# Revit family: Furniture_Chair_YUMI_3
name_source: partatom
category: Furniture
units: mm (PartAtom-declared; Revit-internal decimal feet)

## family parameters
Always vertical = No
Cut with Voids When Loaded = No
OmniClass Number = 23.21.23.15.17
Room Calculation Point = No
Shared = No
Work Plane-Based = Yes

## types (6) — shared parameters
BIMobject category = Chair
BIMobject category code = furniture-chair
BIMobject main category = Furniture
BIMobject main category code = furniture
Brand url = https://www.sandlerseating.com
Default Elevation = 1219.2 mm  [stored 4 ft]
Description = Chair
Design country = UK
Edition number = 1
Heigth Shell = 740 mm  [stored 2.42782 ft]
IFC Classification = Furnishing Element
Manufacturer = Sandler
Manufacturer country = UK
Manufacturer name = Sandler
Masterformat 2014 Code = 12 48 43.13
Masterformat 2014 Description = Chair Mats
OmniClass Code = 23-21 23 15 17
Product Guid = ??
Product data url = https://www.sandlerseating.com
Product family = Furniture
Product group = Chair
Seat = TP01 - YUMI
Uniformat II Description = Movable Furnishings
height = 1020 mm  [stored 3.34646 ft]

## per-type parameters (varying)
| type | Frame | Frame Material | Seat Material | Shell Material | depth | width |
| YUMI 3.6 | BS04 - YUMI | Wood - Wenge Beech | Laminate - Grey | Laminate - Grey | 550 mm | 590 mm  [stored 1.9357 ft] |
| YUMI 3.5 | BS04 - YUMI | Wood - Natural Beech | Leather - Blue - Sandler 145 | Leather - Blue - Sandler 145 | 550 mm | 590 mm  [stored 1.9357 ft] |
| YUMI 3.4 | BS04 - YUMI | Wood - Walnut Beech | Wood - Walnut Beech | Wood - Walnut Beech | 550 mm | 590 mm  [stored 1.9357 ft] |
| YUMI 3.3 | BS03 - YUMI | Wood - Wenge Beech | Laminate - Grey | Laminate - Grey | 520 mm  [stored 1.70604 ft] | 465 mm  [stored 1.52559 ft] |
| YUMI 3.2 | BS03 - YUMI | Wood - Walnut Beech | Wood - Walnut Beech | Wood - Walnut Beech | 520 mm  [stored 1.70604 ft] | 465 mm  [stored 1.52559 ft] |
| YUMI 3.1 | BS03 - YUMI | Wood - Natural Beech | Leather - Tan - Sandler 131 | Leather - Tan - Sandler 131 | 520 mm  [stored 1.70604 ft] | 465 mm  [stored 1.52559 ft] |

note: column(s) folded — value = type name in every type: Model, Product name

note: [stored X ft] marks values corroborated as IEEE doubles in the binary element streams (Revit-internal decimal feet)

## geometry (parser evidence)
native form markers: Sweep x9
no freeform markers — native parametric forms only
